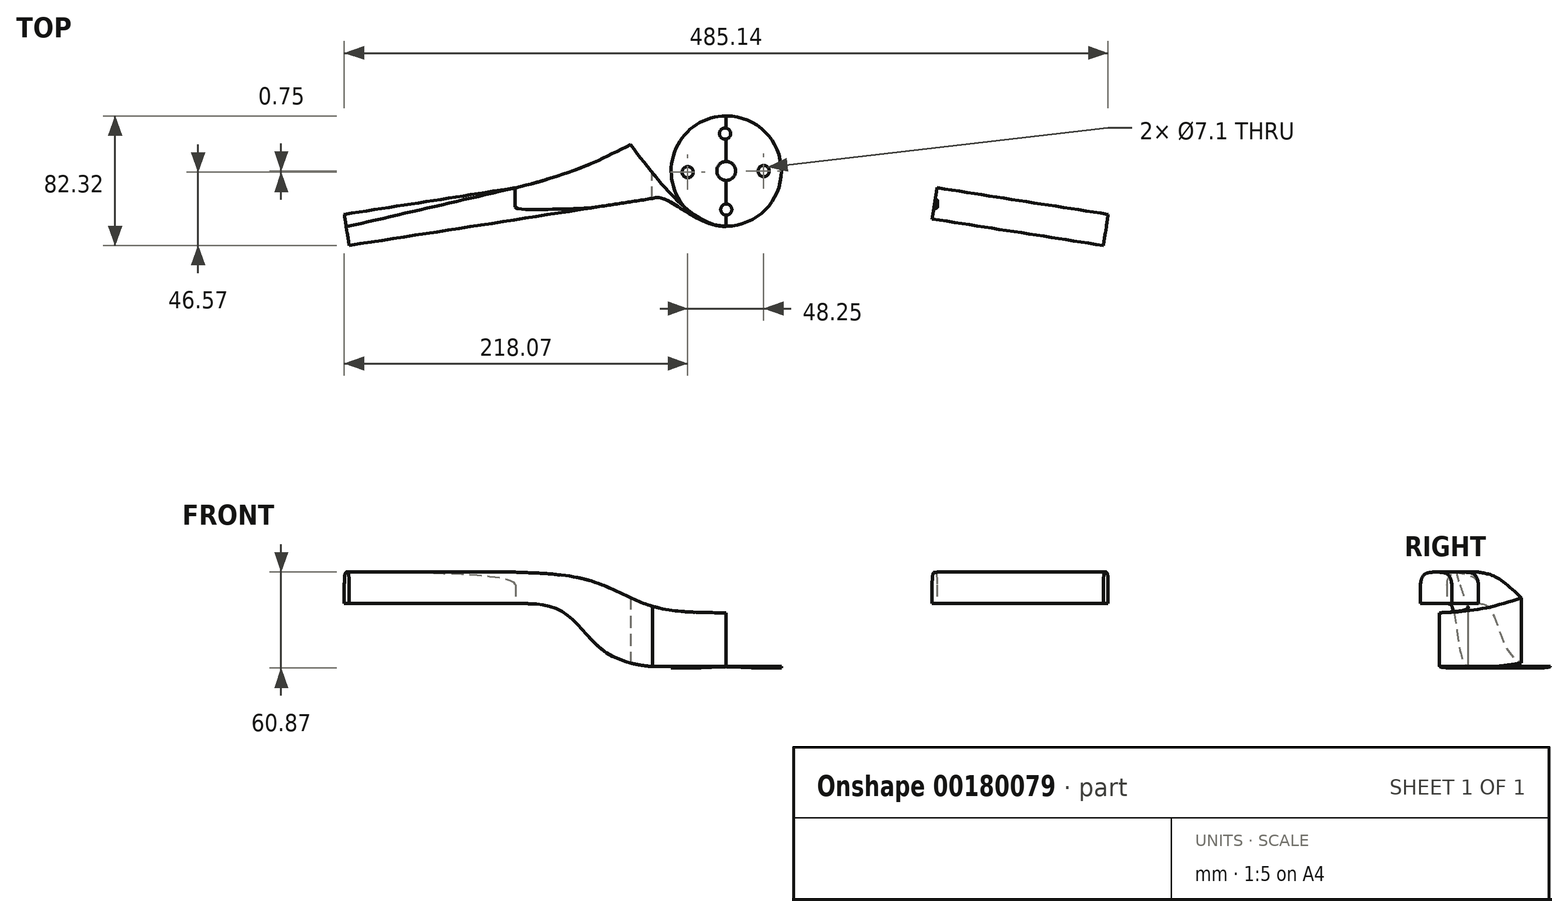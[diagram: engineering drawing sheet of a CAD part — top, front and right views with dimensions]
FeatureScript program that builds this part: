
annotation { "Feature Type Name" : "Feature", "Feature Type Description" : "" }
export const myFeature = defineFeature(function(context is Context, id is Id, definition is map)
    precondition{}
    {
        {
            var Q0;
            Q0=qCreatedBy(makeId("Top.planeOp"),FACE);
            var sketch = newSketch(context, id + "F0", { "sketchPlane" : qUnion([Q0])});
            skCircle(sketch, "E0", {"center": v(0, 0) * mm, "radius": 12.5 * mm});
            skCircle(sketch, "E1", {"center": v(0, 0) * mm, "radius": 35 * mm});
            skLineSegment(sketch, "E2", {"start": v(12.5, 0) * mm, "end": v(35, 0) * mm, "construction": true});
            skLineSegment(sketch, "E3", {"start": v(0, -12.5) * mm, "end": v(0, -35) * mm, "construction": true});
            skLineSegment(sketch, "E4", {"start": v(-12.5, 0) * mm, "end": v(-35, 0) * mm, "construction": true});
            skLineSegment(sketch, "E5", {"start": v(0, 12.5) * mm, "end": v(0, 35) * mm, "construction": true});
            skCircle(sketch, "E6", {"center": v(23.75, 0) * mm, "radius": 3.55 * mm});
            skCircle(sketch, "E7", {"center": v(23.75, 0) * mm, "radius": 6 * mm});
            skCircle(sketch, "E8.1.0", {"center": v(-0.75, 23.75) * mm, "radius": 3.55 * mm});
            skCircle(sketch, "E8.1.1", {"center": v(-0.75, 23.75) * mm, "radius": 6 * mm});
            skCircle(sketch, "E8.2.0", {"center": v(-24.5, -0.75) * mm, "radius": 3.55 * mm});
            skCircle(sketch, "E8.2.1", {"center": v(-24.5, -0.75) * mm, "radius": 6 * mm});
            skCircle(sketch, "E8.3.0", {"center": v(0, -24.5) * mm, "radius": 3.55 * mm});
            skCircle(sketch, "E8.3.1", {"center": v(0, -24.5) * mm, "radius": 6 * mm});
            skPoint(sketch, "E8.center", {"position": v(-0.38, -0.37) * mm});
            skCircle(sketch, "E9", {"center": v(0, 0) * mm, "radius": 3.55 * mm});
            skCircle(sketch, "E10", {"center": v(0, 0) * mm, "radius": 6 * mm});
            skSolve(sketch);
        }
        {
            var Q0;
            Q0=makeQuery(id+"F0.imprint","IMPRINT",FACE,{"disambiguationData":[TD([[makeQuery(id+"F0.imprint","IMPRINT",EDGE,{"derivedFrom":sQuery(id+"F0.wireOp",EDGE,"E0")}),1.0]])]});
            extrude(context, id + "F1", {"entities" : qUnion([Q0]), "depth" : 100 * mm});
        }
        {
            var Q0;
            Q0=makeQuery(id+"F0.imprint","IMPRINT",FACE,{"disambiguationData":[TD([[makeQuery(id+"F0.imprint","IMPRINT",EDGE,{"derivedFrom":sQuery(id+"F0.wireOp",EDGE,"E0")}),-1.0]])]});
            var Q1;
            Q1=makeQuery(id+"F0.imprint","IMPRINT",FACE,{"disambiguationData":[TD([[makeQuery(id+"F0.imprint","IMPRINT",EDGE,{"derivedFrom":sQuery(id+"F0.wireOp",EDGE,"E0")}),1.0]])]});
            var Q2;
            Q2=makeQuery(id+"F0.imprint","IMPRINT",FACE,{"disambiguationData":[TD([[makeQuery(id+"F0.imprint","IMPRINT",EDGE,{"derivedFrom":sQuery(id+"F0.wireOp",EDGE,"E8.2.0")}),-1.0]])]});
            var Q3;
            Q3=makeQuery(id+"F0.imprint","IMPRINT",FACE,{"disambiguationData":[TD([[makeQuery(id+"F0.imprint","IMPRINT",EDGE,{"derivedFrom":sQuery(id+"F0.wireOp",EDGE,"E8.3.0")}),-1.0]])]});
            var Q4;
            Q4=makeQuery(id+"F0.imprint","IMPRINT",FACE,{"disambiguationData":[TD([[makeQuery(id+"F0.imprint","IMPRINT",EDGE,{"derivedFrom":sQuery(id+"F0.wireOp",EDGE,"E6")}),-1.0]])]});
            var Q5;
            Q5=makeQuery(id+"F0.imprint","IMPRINT",FACE,{"disambiguationData":[TD([[makeQuery(id+"F0.imprint","IMPRINT",EDGE,{"derivedFrom":sQuery(id+"F0.wireOp",EDGE,"E8.1.0")}),-1.0]])]});
            var Q6;
            Q6=makeQuery(id+"F0.imprint","IMPRINT",FACE,{"disambiguationData":[TD([[makeQuery(id+"F0.imprint","IMPRINT",EDGE,{"derivedFrom":sQuery(id+"F0.wireOp",EDGE,"E9")}),-1.0]])]});
            extrude(context, id + "F2", {"entities" : qUnion([Q0, Q1, Q2, Q3, Q4, Q5, Q6]), "operationType" : NewBodyOperationType.ADD, "oppositeDirection" : true, "depth" : 20 * mm});
        }
        {
            var Q0;
            Q0=makeQuery(id+"F2.opExtrude","CAP_FACE",FACE,{"disambiguationData":[OSD([sQuery(id+"F0.wireOp",EDGE,"E1")])],"isStart":false});
            extrude(context, id + "F3", {"entities" : qUnion([Q0]), "operationType" : NewBodyOperationType.ADD, "oppositeDirection" : true, "depth" : 138 * mm, "hasSecondDirection" : true, "secondDirectionOppositeDirection" : true, "secondDirectionDepth" : 118 * mm});
        }
        {
            var Q0;
            Q0=makeQuery(id+"F0.imprint","IMPRINT",FACE,{"disambiguationData":[TD([[makeQuery(id+"F0.imprint","IMPRINT",EDGE,{"derivedFrom":sQuery(id+"F0.wireOp",EDGE,"E6")}),-1.0]])]});
            var Q1;
            Q1=makeQuery(id+"F0.imprint","IMPRINT",FACE,{"disambiguationData":[TD([[makeQuery(id+"F0.imprint","IMPRINT",EDGE,{"derivedFrom":sQuery(id+"F0.wireOp",EDGE,"E8.1.0")}),-1.0]])]});
            var Q2;
            Q2=makeQuery(id+"F0.imprint","IMPRINT",FACE,{"disambiguationData":[TD([[makeQuery(id+"F0.imprint","IMPRINT",EDGE,{"derivedFrom":sQuery(id+"F0.wireOp",EDGE,"E8.2.0")}),-1.0]])]});
            var Q3;
            Q3=makeQuery(id+"F0.imprint","IMPRINT",FACE,{"disambiguationData":[TD([[makeQuery(id+"F0.imprint","IMPRINT",EDGE,{"derivedFrom":sQuery(id+"F0.wireOp",EDGE,"E8.3.0")}),-1.0]])]});
            extrude(context, id + "F4", {"entities" : qUnion([Q0, Q1, Q2, Q3]), "operationType" : NewBodyOperationType.REMOVE, "oppositeDirection" : true, "depth" : 5 * mm});
        }
        {
            var Q0;
            Q0=makeQuery(id+"F0.imprint","IMPRINT",FACE,{"disambiguationData":[TD([[makeQuery(id+"F0.imprint","IMPRINT",EDGE,{"derivedFrom":sQuery(id+"F0.wireOp",EDGE,"E6")}),-1.0]])]});
            var Q1;
            Q1=makeQuery(id+"F0.imprint","IMPRINT",FACE,{"disambiguationData":[TD([[makeQuery(id+"F0.imprint","IMPRINT",EDGE,{"derivedFrom":sQuery(id+"F0.wireOp",EDGE,"E8.1.0")}),-1.0]])]});
            var Q2;
            Q2=makeQuery(id+"F0.imprint","IMPRINT",FACE,{"disambiguationData":[TD([[makeQuery(id+"F0.imprint","IMPRINT",EDGE,{"derivedFrom":sQuery(id+"F0.wireOp",EDGE,"E8.2.0")}),-1.0]])]});
            var Q3;
            Q3=makeQuery(id+"F0.imprint","IMPRINT",FACE,{"disambiguationData":[TD([[makeQuery(id+"F0.imprint","IMPRINT",EDGE,{"derivedFrom":sQuery(id+"F0.wireOp",EDGE,"E8.3.0")}),-1.0]])]});
            extrude(context, id + "F5", {"entities" : qUnion([Q0, Q1, Q2, Q3]), "operationType" : NewBodyOperationType.REMOVE, "depth" : 103 * mm});
        }
        {
            var Q0;
            Q0=makeQuery(id+"F0.imprint","IMPRINT",FACE,{"disambiguationData":[TD([[makeQuery(id+"F0.imprint","IMPRINT",EDGE,{"derivedFrom":sQuery(id+"F0.wireOp",EDGE,"E9")}),-1.0]])]});
            extrude(context, id + "F6", {"entities" : qUnion([Q0]), "operationType" : NewBodyOperationType.REMOVE, "depth" : 118 * mm, "hasSecondDirection" : true, "secondDirectionOppositeDirection" : false, "secondDirectionDepth" : 107 * mm});
        }
        {
            var Q0;
            Q0=qCreatedBy(makeId("Front.planeOp"),FACE);
            var sketch = newSketch(context, id + "F7", { "sketchPlane" : qUnion([Q0])});
            skLineSegment(sketch, "E11", {"start": v(-14, 49) * mm, "end": v(-7, 49) * mm});
            skLineSegment(sketch, "E12", {"start": v(-7, 49) * mm, "end": v(-7, 39) * mm});
            skLineSegment(sketch, "E13", {"start": v(-7, 39) * mm, "end": v(0, 39) * mm});
            skLineSegment(sketch, "E14", {"start": v(0, 39) * mm, "end": v(0, 59) * mm});
            skLineSegment(sketch, "E15", {"start": v(0, 59) * mm, "end": v(7, 59) * mm});
            skLineSegment(sketch, "E16", {"start": v(7, 59) * mm, "end": v(7, 49) * mm});
            skLineSegment(sketch, "E17", {"start": v(7, 49) * mm, "end": v(14, 49) * mm});
            skLineSegment(sketch, "E18.0", {"start": v(6.55, 48.6) * mm, "end": v(14, 48.6) * mm});
            skLineSegment(sketch, "E18.1", {"start": v(-14, 48.6) * mm, "end": v(-7.4, 48.6) * mm});
            skLineSegment(sketch, "E18.2", {"start": v(-7.4, 48.6) * mm, "end": v(-7.4, 38.6) * mm});
            skLineSegment(sketch, "E18.3", {"start": v(-7.4, 38.6) * mm, "end": v(0.4, 38.6) * mm});
            skLineSegment(sketch, "E18.4", {"start": v(0.4, 38.6) * mm, "end": v(0.4, 48.6) * mm});
            skLineSegment(sketch, "E19", {"start": v(0.4, 48.6) * mm, "end": v(0.4, 58.53) * mm});
            skLineSegment(sketch, "E20", {"start": v(0.4, 58.53) * mm, "end": v(6.55, 58.53) * mm});
            skLineSegment(sketch, "E21", {"start": v(6.55, 58.53) * mm, "end": v(6.55, 48.6) * mm});
            skLineSegment(sketch, "E22", {"start": v(14, 49) * mm, "end": v(14, 48.6) * mm});
            skLineSegment(sketch, "E23", {"start": v(-14, 48.6) * mm, "end": v(-14, 49) * mm});
            skSolve(sketch);
        }
        {
            var Q0;
            Q0=makeQuery(id+"F7.imprint","IMPRINT",FACE,{"disambiguationData":[TD([[makeQuery(id+"F7.imprint","IMPRINT",EDGE,{"derivedFrom":sQuery(id+"F7.wireOp",EDGE,"E11")}),-1.0]])]});
            extrude(context, id + "F8", {"entities" : qUnion([Q0]), "operationType" : NewBodyOperationType.REMOVE, "endBound" : BoundingType.SYMMETRIC, "oppositeDirection" : true, "depth" : 30 * mm});
        }
        {
            var Q0;
            Q0=makeQuery(id+"F3.opExtrude","CAP_FACE",FACE,{"disambiguationData":[OSD([sQuery(id+"F0.wireOp",EDGE,"E1"),sQuery(id+"F0.wireOp",EDGE,"E6"),sQuery(id+"F0.wireOp",EDGE,"E8.1.0"),sQuery(id+"F0.wireOp",EDGE,"E8.2.0"),sQuery(id+"F0.wireOp",EDGE,"E8.3.0"),sQuery(id+"F0.wireOp",EDGE,"E9")])],"isStart":false});
            cPlane(context, id + "F9", {"entities" : qUnion([Q0]), "cplaneType" : CPlaneType.OFFSET, "offset" : 0 * mm, "oppositeDirection" : true, "width" : 150 * mm, "height" : 150 * mm});
        }
        {
            var Q0;
            Q0=qCreatedBy(id+"F9.planeOp",FACE);
            var sketch = newSketch(context, id + "F10", { "sketchPlane" : qUnion([Q0])});
            skLineSegment(sketch, "E24", {"start": v(0, 0) * mm, "end": v(-160, 0) * mm, "construction": true});
            skLineSegment(sketch, "E25", {"start": v(0, 0) * mm, "end": v(0, 78.57) * mm, "construction": true});
            skLineSegment(sketch, "E26.MirrorCS", {"start": v(0, 0) * mm, "end": v(160, 0) * mm, "construction": true});
            skLineSegment(sketch, "E27", {"start": v(0, 0) * mm, "end": v(-241.03, -37.43) * mm, "construction": true});
            skLineSegment(sketch, "E28.MirrorCS", {"start": v(0, 0) * mm, "end": v(241.03, -37.43) * mm, "construction": true});
            skLineSegment(sketch, "E29", {"start": v(-241.03, -37.43) * mm, "end": v(-242.57, -27.55) * mm});
            skLineSegment(sketch, "E30", {"start": v(-242.57, -27.55) * mm, "end": v(-133.87, -10.67) * mm});
            skLineSegment(sketch, "E31", {"start": v(-133.87, -10.67) * mm, "end": v(-132.33, -20.55) * mm});
            skLineSegment(sketch, "E32.MirrorCS", {"start": v(-239.5, -47.32) * mm, "end": v(-130.8, -30.43) * mm});
            skLineSegment(sketch, "E33.MirrorCS", {"start": v(-241.03, -37.43) * mm, "end": v(-239.5, -47.32) * mm});
            skLineSegment(sketch, "E34.MirrorCS", {"start": v(-130.8, -30.43) * mm, "end": v(-132.33, -20.55) * mm});
            skFitSpline(sketch, "E35", {"points": [v(-133.87, -10.67) * mm, v(-85, 5) * mm, v(-58.94, 17.6) * mm, v(0, 34.98) * mm], "startDerivative": vector(141.92, 32.75) * mm, "endDerivative": vector(122.66, -6.76) * mm});
            skLineSegment(sketch, "E36", {"start": v(-130.8, -30.43) * mm, "end": v(-46.91, -17.4) * mm});
            skFitSpline(sketch, "E37", {"points": [v(-46.91, -17.4) * mm, v(-39.06, -17.87) * mm, v(0, -35.26) * mm, v(66.63, 24.58) * mm], "startDerivative": vector(43.69, 10.02) * mm, "endDerivative": vector(132.17, 177.96) * mm});
            skLineSegment(sketch, "E38", {"start": v(0, 0) * mm, "end": v(0, -35.26) * mm, "construction": true});
            skFitSpline(sketch, "E39.MirrorCS", {"points": [v(133.87, -10.67) * mm, v(85, 5) * mm, v(58.94, 17.6) * mm, v(0, 34.98) * mm], "startDerivative": vector(-141.92, 32.75) * mm, "endDerivative": vector(-122.66, -6.76) * mm});
            skLineSegment(sketch, "E40.MirrorCS", {"start": v(130.8, -30.43) * mm, "end": v(46.91, -17.4) * mm});
            skFitSpline(sketch, "E41.MirrorCS", {"points": [v(46.91, -17.4) * mm, v(39.06, -17.87) * mm, v(0, -35.26) * mm, v(-66.63, 24.58) * mm], "startDerivative": vector(-43.69, 10.02) * mm, "endDerivative": vector(-132.17, 177.96) * mm});
            skLineSegment(sketch, "E42.MirrorCS", {"start": v(242.57, -27.55) * mm, "end": v(133.87, -10.67) * mm});
            skLineSegment(sketch, "E43.MirrorCS", {"start": v(241.03, -37.43) * mm, "end": v(242.57, -27.55) * mm});
            skLineSegment(sketch, "E44.MirrorCS", {"start": v(239.5, -47.32) * mm, "end": v(130.8, -30.43) * mm});
            skLineSegment(sketch, "E45.MirrorCS", {"start": v(133.87, -10.67) * mm, "end": v(132.33, -20.55) * mm});
            skLineSegment(sketch, "E46.MirrorCS", {"start": v(241.03, -37.43) * mm, "end": v(239.5, -47.32) * mm});
            skLineSegment(sketch, "E47.MirrorCS", {"start": v(130.8, -30.43) * mm, "end": v(132.33, -20.55) * mm});
            skSolve(sketch);
        }
        {
            var Q0;
            Q0=makeQuery(id+"F10.imprint","IMPRINT",FACE,{"disambiguationData":[TD([[makeQuery(id+"F10.imprint","IMPRINT",EDGE,{"derivedFrom":sQuery(id+"F10.wireOp",EDGE,"E31")}),1.0]])]});
            var Q1;
            Q1=makeQuery(id+"F10.imprint","IMPRINT",FACE,{"disambiguationData":[TD([[makeQuery(id+"F10.imprint","IMPRINT",EDGE,{"derivedFrom":sQuery(id+"F10.wireOp",EDGE,"E29")}),-1.0]])]});
            var Q2;
            Q2=makeQuery(id+"F10.imprint","IMPRINT",FACE,{"disambiguationData":[TD([[makeQuery(id+"F10.imprint","IMPRINT",EDGE,{"derivedFrom":sQuery(id+"F10.wireOp",EDGE,"E42.MirrorCS")}),1.0]])]});
            extrude(context, id + "F11", {"entities" : qUnion([Q0, Q1, Q2]), "depth" : 60 * mm});
        }
        {
            var Q0;
            Q0=qCreatedBy(makeId("Front.planeOp"),FACE);
            var sketch = newSketch(context, id + "F12", { "sketchPlane" : qUnion([Q0])});
            skLineSegment(sketch, "E48", {"start": v(0, 0) * mm, "end": v(0, 178) * mm, "construction": true});
            skLineSegment(sketch, "E49", {"start": v(-134.15, 178) * mm, "end": v(-243.43, 178) * mm});
            skLineSegment(sketch, "E50", {"start": v(-243.43, 178) * mm, "end": v(-243.43, 158) * mm});
            skLineSegment(sketch, "E51", {"start": v(-243.43, 158) * mm, "end": v(-133.43, 158) * mm});
            skLineSegment(sketch, "E52", {"start": v(-133.43, 158) * mm, "end": v(-133.43, 118) * mm, "construction": true});
            skFitSpline(sketch, "E53", {"points": [v(-133.43, 158) * mm, v(-104.33, 153.16) * mm, v(-79.28, 129.23) * mm, v(-47.2, 118) * mm, v(0, 118) * mm], "startDerivative": vector(137.02, 1.05) * mm, "endDerivative": vector(171.62, 7.87) * mm});
            skFitSpline(sketch, "E54", {"points": [v(-134.15, 178) * mm, v(-84.96, 172.15) * mm, v(-47.43, 156.5) * mm, v(0, 152.24) * mm], "startDerivative": vector(149.56, -5.25) * mm, "endDerivative": vector(146.62, -0.13) * mm});
            skFitSpline(sketch, "E55.MirrorCS", {"points": [v(134.15, 178) * mm, v(84.96, 172.15) * mm, v(47.43, 156.5) * mm, v(0, 152.24) * mm], "startDerivative": vector(-149.56, -5.25) * mm, "endDerivative": vector(-146.62, -0.13) * mm});
            skFitSpline(sketch, "E56.MirrorCS", {"points": [v(133.43, 158) * mm, v(104.33, 153.16) * mm, v(79.28, 129.23) * mm, v(47.2, 118) * mm, v(0, 118) * mm], "startDerivative": vector(-137.02, 1.05) * mm, "endDerivative": vector(-171.62, 7.87) * mm});
            skLineSegment(sketch, "E57.MirrorCS", {"start": v(243.43, 158) * mm, "end": v(133.43, 158) * mm});
            skLineSegment(sketch, "E58.MirrorCS", {"start": v(243.43, 178) * mm, "end": v(243.43, 158) * mm});
            skLineSegment(sketch, "E59.MirrorCS", {"start": v(134.15, 178) * mm, "end": v(243.43, 178) * mm});
            skPoint(sketch, "E60.orphan", {"position": v(0, 178) * mm});
            skSolve(sketch);
        }
        {
            var Q0;
            Q0=makeQuery(id+"F12.imprint","IMPRINT",FACE,{"disambiguationData":[TD([[makeQuery(id+"F12.imprint","IMPRINT",EDGE,{"derivedFrom":sQuery(id+"F12.wireOp",EDGE,"E49")}),1.0]])]});
            extrude(context, id + "F13", {"entities" : qUnion([Q0]), "operationType" : NewBodyOperationType.INTERSECT, "endBound" : BoundingType.SYMMETRIC, "depth" : 100 * mm});
        }
        {
            var Q0;
            Q0=makeQuery(id+"F11.opExtrude","CAP_EDGE",EDGE,{"disambiguationData":[OSD([sQuery(id+"F10.wireOp",EDGE,"E30")])],"isStart":false});
            var Q1;
            Q1=makeQuery(id+"F11.opExtrude","CAP_EDGE",EDGE,{"disambiguationData":[OSD([sQuery(id+"F10.wireOp",EDGE,"E32.MirrorCS"),sQuery(id+"F10.wireOp",EDGE,"E36")])],"isStart":false});
            var Q2;
            Q2=makeQuery(id+"F13.boolean.opBoolean","INTERSECT",EDGE,{"derivedFrom":[makeQuery(id+"F11.opExtrude","SWEPT_FACE",FACE,{"disambiguationData":[OSD([sQuery(id+"F10.wireOp",EDGE,"E30")])]}),makeQuery(id+"F13.boolean.toolComplement.opBoolean","COPY",FACE,{"derivedFrom":makeQuery(id+"F13.opExtrude","SWEPT_FACE",FACE,{"disambiguationData":[OSD([sQuery(id+"F12.wireOp",EDGE,"E51")])]})})]});
            var Q3;
            Q3=makeQuery(id+"F11.opExtrude","CAP_EDGE",EDGE,{"disambiguationData":[OSD([sQuery(id+"F10.wireOp",EDGE,"E42.MirrorCS")])],"isStart":false});
            var Q4;
            Q4=makeQuery(id+"F11.opExtrude","CAP_EDGE",EDGE,{"disambiguationData":[OSD([sQuery(id+"F10.wireOp",EDGE,"E40.MirrorCS"),sQuery(id+"F10.wireOp",EDGE,"E44.MirrorCS")])],"isStart":false});
            var Q5;
            Q5=makeQuery(id+"F13.boolean.opBoolean","INTERSECT",EDGE,{"derivedFrom":[makeQuery(id+"F11.opExtrude","SWEPT_FACE",FACE,{"disambiguationData":[OSD([sQuery(id+"F10.wireOp",EDGE,"E42.MirrorCS")])]}),makeQuery(id+"F13.boolean.toolComplement.opBoolean","COPY",FACE,{"derivedFrom":makeQuery(id+"F13.opExtrude","SWEPT_FACE",FACE,{"disambiguationData":[OSD([sQuery(id+"F12.wireOp",EDGE,"E57.MirrorCS")])]})})]});
            fillet(context, id + "F14", {"entities" : qUnion([Q0, Q1, Q2, Q3, Q4, Q5]), "radius" : 8 * mm, "tangentPropagation" : true, "rho" : 0.5, "crossSection" : FilletCrossSection.CONIC, "allowEdgeOverflow" : false});
        }
    });
